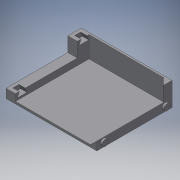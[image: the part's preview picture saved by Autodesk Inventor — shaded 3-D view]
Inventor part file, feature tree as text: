
AUTODESK INVENTOR PART (.ipt)
format: ipt  version: 2016 SP2 (Build 200236200, 236)  size: 176,640 bytes
history: native  units: mm
features: reference x17, extrude x5, sketch x5, chamfer x2
ambient origin geometry x8: Origin, YZ Plane, XZ Plane, XY Plane, X Axis, Y Axis, Z Axis, Center Point
bodies: Volumenkörper1 (feature_tree)
feature tree (29):
  extrude  "Extrusion1"  Depth=0.05mm
  extrude  "Extrusion2"  Depth=0.1mm
  extrude  "Extrusion3"  Depth=0.1mm
  extrude  "Extrusion4"  Depth=0.1mm
  extrude  "Extrusion5"  Depth=3.4mm TaperAngle=0.0deg
  chamfer  "Fase2"  Distance=2.5mm
  chamfer  "Fase3"  Distance=2.0mm
  sketch  "Skizze1"  dims[d0=0.2mm d1=0.05mm]
  reference  "Referenz1"
  reference  "Referenz2"
  reference  "Referenz3"
  reference  "Referenz4"
  reference  "Referenz5"
  reference  "Referenz6"
  reference  "Referenz7"
  reference  "Referenz8"
  reference  "Referenz9"
  reference  "Referenz10"
  reference  "Referenz11"
  reference  "Referenz12"
  reference  "Referenz13"
  sketch  "Skizze2"  dims[d2=0.05mm d3=0.1mm]
  sketch  "Skizze3"  dims[d4=0.2mm d5=0.1mm]
  sketch  "Skizze4"  dims[d6=0.1mm d7=0.1mm]
  reference  "Referenz14"
  reference  "Referenz15"
  sketch  "Skizze5"  dims[d8=7.0mm d9=0.0mm d10=3.4mm d11=0.0mm d12=2.5mm d13=2.0mm d14=2.0mm d15=89.5mm d16=0.0mm d17=0.05mm d18=0.05mm d19=2.0mm d20=0.0mm d22=7.0mm d23=0.0mm d27=4.0mm d28=6.5mm d29=2.0mm d30=45.0deg d31=7.0mm d32=6.5mm d33=2.0mm d34=45.0deg]
  reference  "Referenz16"
  reference  "Referenz17"
